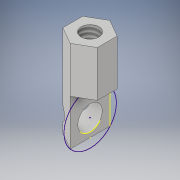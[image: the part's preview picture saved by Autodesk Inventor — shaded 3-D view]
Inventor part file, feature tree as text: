
AUTODESK INVENTOR PART (.ipt)
format: ipt  version: 2018 (Build 220112000, 112)  size: 144,896 bytes
history: native  units: in
note: dims shown in document units (in); Inventor stores cm internally (conversion verified against a paired STEP export)
features: sketch x5, extrude x2, hole x2
ambient origin geometry x8: Origin, YZ Plane, XZ Plane, XY Plane, X Axis, Y Axis, Z Axis, Center Point
bodies: Solid1 (feature_tree)
feature tree (9):
  extrude  "Extrusion1"  TaperAngle=90.0deg  [1 undecoded]
  hole  "Hole1"  [1 undecoded]
  extrude  "Extrusion2"  Depth=0.5in TaperAngle=0.0deg
  hole  "Hole2"  [1 undecoded]
  sketch  "Sketch7"  dims[d19=0.266in d20=0.5in d21=0.507in d22=0.25in d23=0.5635in d24=1.0in d25=0.8108in]
  sketch  "Sketch1"  dims[d0=0.1875in d1=90.0deg]
  sketch  "Sketch2"  dims[d2=2.3622in d4=360.0deg d6=1.0in d7=0.0in]
  sketch  "Sketch3"  dims[d8=0.196in d9=0.25in d10=0.375in d11=0.25in d12=0.5635in d13=0.5in d14=0.8108in d15=0.5in d16=0.0in]
  sketch  "Sketch5"  dims[d17=0.1875in d18=0.266in]
note: 3 required parameter values undecoded (feature->parameter linkage not recoverable at this tier; creation-order binding heuristic only, values carry confidence <= 0.55)
